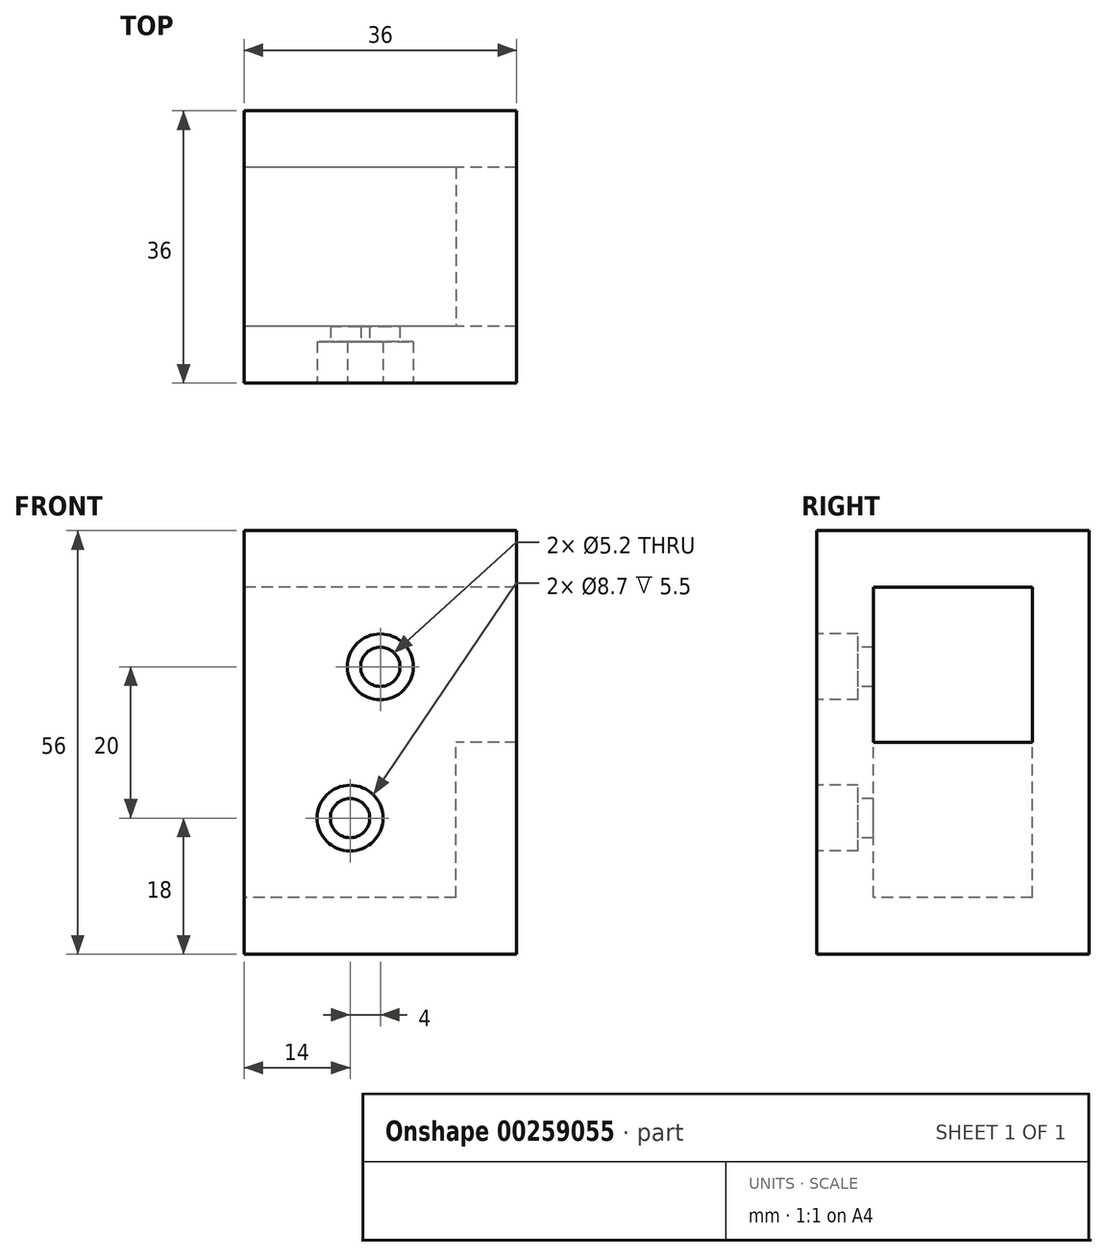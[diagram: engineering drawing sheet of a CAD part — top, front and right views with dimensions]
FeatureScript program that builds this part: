
annotation { "Feature Type Name" : "Feature", "Feature Type Description" : "" }
export const myFeature = defineFeature(function(context is Context, id is Id, definition is map)
    precondition{}
    {
        {
            var Q0;
            Q0=qCreatedBy(makeId("Top.planeOp"),FACE);
            var sketch = newSketch(context, id + "F0", { "sketchPlane" : qUnion([Q0])});
            skLineSegment(sketch, "E0.bottom", {"start": v(0, 36) * mm, "end": v(36, 36) * mm});
            skLineSegment(sketch, "E0.top", {"start": v(0, 0) * mm, "end": v(36, 0) * mm});
            skLineSegment(sketch, "E0.left", {"start": v(0, 36) * mm, "end": v(0, 0) * mm});
            skLineSegment(sketch, "E0.right", {"start": v(36, 36) * mm, "end": v(36, 0) * mm});
            skSolve(sketch);
        }
        {
            var Q0;
            Q0 = qSketchRegion(id + "F0", true);
            extrude(context, id + "F1", {"entities" : qUnion([Q0]), "depth" : 56 * mm});
        }
        {
            var Q0;
            Q0=makeQuery(id+"F1.opExtrude","SWEPT_FACE",FACE,{"disambiguationData":[OSD([sQuery(id+"F0.wireOp",EDGE,"E0.left")])]});
            var sketch = newSketch(context, id + "F2", { "sketchPlane" : qUnion([Q0])});
            skLineSegment(sketch, "E1.bottom", {"start": v(-28.5, 7.5) * mm, "end": v(-7.5, 7.5) * mm});
            skLineSegment(sketch, "E1.top", {"start": v(-28.5, 48.5) * mm, "end": v(-7.5, 48.5) * mm});
            skLineSegment(sketch, "E1.left", {"start": v(-28.5, 7.5) * mm, "end": v(-28.5, 48.5) * mm});
            skLineSegment(sketch, "E1.right", {"start": v(-7.5, 7.5) * mm, "end": v(-7.5, 48.5) * mm});
            skSolve(sketch);
        }
        {
            var Q0;
            Q0 = qSketchRegion(id + "F2", true);
            extrude(context, id + "F3", {"entities" : qUnion([Q0]), "operationType" : NewBodyOperationType.REMOVE, "oppositeDirection" : true, "depth" : 28 * mm});
        }
        {
            var Q0;
            Q0=makeQuery(id+"F1.opExtrude","SWEPT_FACE",FACE,{"disambiguationData":[OSD([sQuery(id+"F0.wireOp",EDGE,"E0.left")])]});
            var sketch = newSketch(context, id + "F4", { "sketchPlane" : qUnion([Q0])});
            skLineSegment(sketch, "E2.bottom", {"start": v(-28.5, 48.5) * mm, "end": v(-7.5, 48.5) * mm});
            skLineSegment(sketch, "E2.top", {"start": v(-28.5, 28) * mm, "end": v(-7.5, 28) * mm});
            skLineSegment(sketch, "E2.left", {"start": v(-28.5, 48.5) * mm, "end": v(-28.5, 28) * mm});
            skLineSegment(sketch, "E2.right", {"start": v(-7.5, 48.5) * mm, "end": v(-7.5, 28) * mm});
            skSolve(sketch);
        }
        {
            var Q0;
            Q0 = qSketchRegion(id + "F4", true);
            extrude(context, id + "F5", {"entities" : qUnion([Q0]), "operationType" : NewBodyOperationType.REMOVE, "oppositeDirection" : true, "depth" : 70 * mm});
        }
        {
            var Q0;
            Q0=makeQuery(id+"F1.opExtrude","SWEPT_FACE",FACE,{"disambiguationData":[OSD([sQuery(id+"F0.wireOp",EDGE,"E0.top")])]});
            var sketch = newSketch(context, id + "F6", { "sketchPlane" : qUnion([Q0])});
            skCircle(sketch, "E3", {"center": v(18, 38) * mm, "radius": 2.6 * mm});
            skCircle(sketch, "E4", {"center": v(14, 18) * mm, "radius": 2.6 * mm});
            skLineSegment(sketch, "E5", {"start": v(0, 28) * mm, "end": v(36, 28) * mm, "construction": true});
            skSolve(sketch);
        }
        {
            var Q0;
            Q0 = qSketchRegion(id + "F6", true);
            extrude(context, id + "F7", {"entities" : qUnion([Q0]), "operationType" : NewBodyOperationType.REMOVE, "oppositeDirection" : true, "depth" : 20 * mm});
        }
        {
            var Q0;
            Q0=makeQuery(id+"F1.opExtrude","SWEPT_FACE",FACE,{"disambiguationData":[OSD([sQuery(id+"F0.wireOp",EDGE,"E0.top")])]});
            var sketch = newSketch(context, id + "F8", { "sketchPlane" : qUnion([Q0])});
            skCircle(sketch, "E6", {"center": v(18, 38) * mm, "radius": 4.35 * mm});
            skCircle(sketch, "E7", {"center": v(14, 18) * mm, "radius": 4.35 * mm});
            skSolve(sketch);
        }
        {
            var Q0;
            Q0 = qSketchRegion(id + "F8", true);
            extrude(context, id + "F9", {"entities" : qUnion([Q0]), "operationType" : NewBodyOperationType.REMOVE, "oppositeDirection" : true, "depth" : 5.5 * mm});
        }
    });
